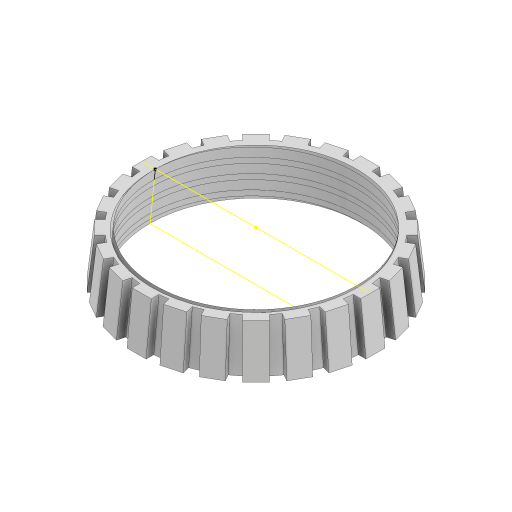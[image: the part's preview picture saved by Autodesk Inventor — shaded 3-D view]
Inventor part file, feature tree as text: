
AUTODESK INVENTOR PART (.ipt)
format: ipt  version: 2023 (Build 270158000, 158)  size: 470,528 bytes
history: native  units: mm
features: sketch x5, draft x2, helix x2, extrude x1, sweep x1, pattern_circular x1
ambient origin geometry x8: Origin, YZ Plane, XZ Plane, XY Plane, X Axis, Y Axis, Z Axis, Center Point
bodies: Solid1 (feature_tree)
feature tree (12):
  extrude  "Extrusion1"  Depth=6.52mm TaperAngle=0.0deg
  draft  "FaceDraft1"
  sketch  "Sketch2"  dims[d7=2.0mm d8=9.0mm d9=10.0mm d10=1.047198mm d11=90.0deg d12=90.0deg d13=0.0mm d14=0.0mm d15=2.0mm d16=3.0mm d17=10.0mm d18=-1.047198mm d19=90.0deg d20=90.0deg d21=0.0mm d22=0.0mm d23=1.5mm d91=1.047198mm]
  sketch  "Sketch4"  dims[d101=2.5mm d102=1.0mm]
  helix  "Coil1"  [1 undecoded]
  helix  "Coil2"  [1 undecoded]
  draft  "FaceDraft2"
  sweep  "Sweep2"
  pattern_circular  "Circular Pattern4"  Count=24 Angle=360.0deg
  sketch  "Sketch1"  dims[d0=26.5mm d2=6.52mm d3=0.0mm d4=1.047198mm]
  sketch  "Sketch9"  dims[d103=0.0mm d104=0.0mm d105=240.0mm d106=360.0deg]
  sketch  "Sketch11"
note: 2 required parameter values undecoded (feature->parameter linkage not recoverable at this tier; creation-order binding heuristic only, values carry confidence <= 0.55)
